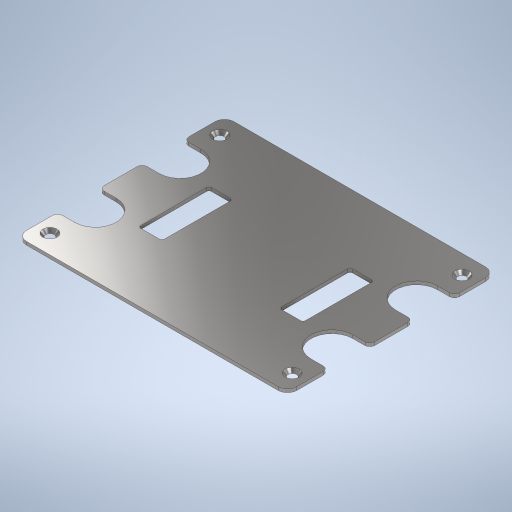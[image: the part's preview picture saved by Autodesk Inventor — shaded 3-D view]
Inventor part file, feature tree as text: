
AUTODESK INVENTOR PART (.ipt)
format: ipt  version: 2023 (Build 270158000, 158)  size: 370,176 bytes
history: native  units: in
note: dims shown in document units (in); Inventor stores cm internally (conversion verified against a paired STEP export)
features: extrude x3, sketch x3, hole x1, fillet x1
ambient origin geometry x8: Origin, YZ Plane, XZ Plane, XY Plane, X Axis, Y Axis, Z Axis, Center Point
bodies: Solid1 (feature_tree)
feature tree (8):
  extrude  "Extrusion1"  Depth=2.2638in
  hole  "Hole1"  [1 undecoded]
  extrude  "Extrusion2"  Depth=0.5906in
  extrude  "Extrusion5"  TaperAngle=0.0deg  [1 undecoded]
  fillet  "Fillet2"  Radius=0.1969in
  sketch  "Sketch1"  dims[d0=1.7362in d1=2.2638in]
  sketch  "Sketch2"  dims[d2=0.0787in d3=0.0276in d4=0.0in]
  sketch  "Sketch8"  dims[d9=0.07in d10=0.146in d11=0.119in d12=0.25in d13=0.5635in d14=1.0in d15=0.8108in d18=0.5906in d19=0.0in d20=0.0in d21=0.1969in d72=1.1811in d73=0.5906in d76=2.0276in d77=1.4213in d78=0.7106in d79=1.0138in d85=0.0197in d88=0.0197in d89=0.0197in d90=0.0197in d91=0.1969in d92=0.5906in d93=0.35in d94=0.3543in d95=0.35in d96=0.3543in d97=0.1417in d98=0.0in d99=0.0in d100=0.0394in]
note: 2 required parameter values undecoded (feature->parameter linkage not recoverable at this tier; creation-order binding heuristic only, values carry confidence <= 0.55)
